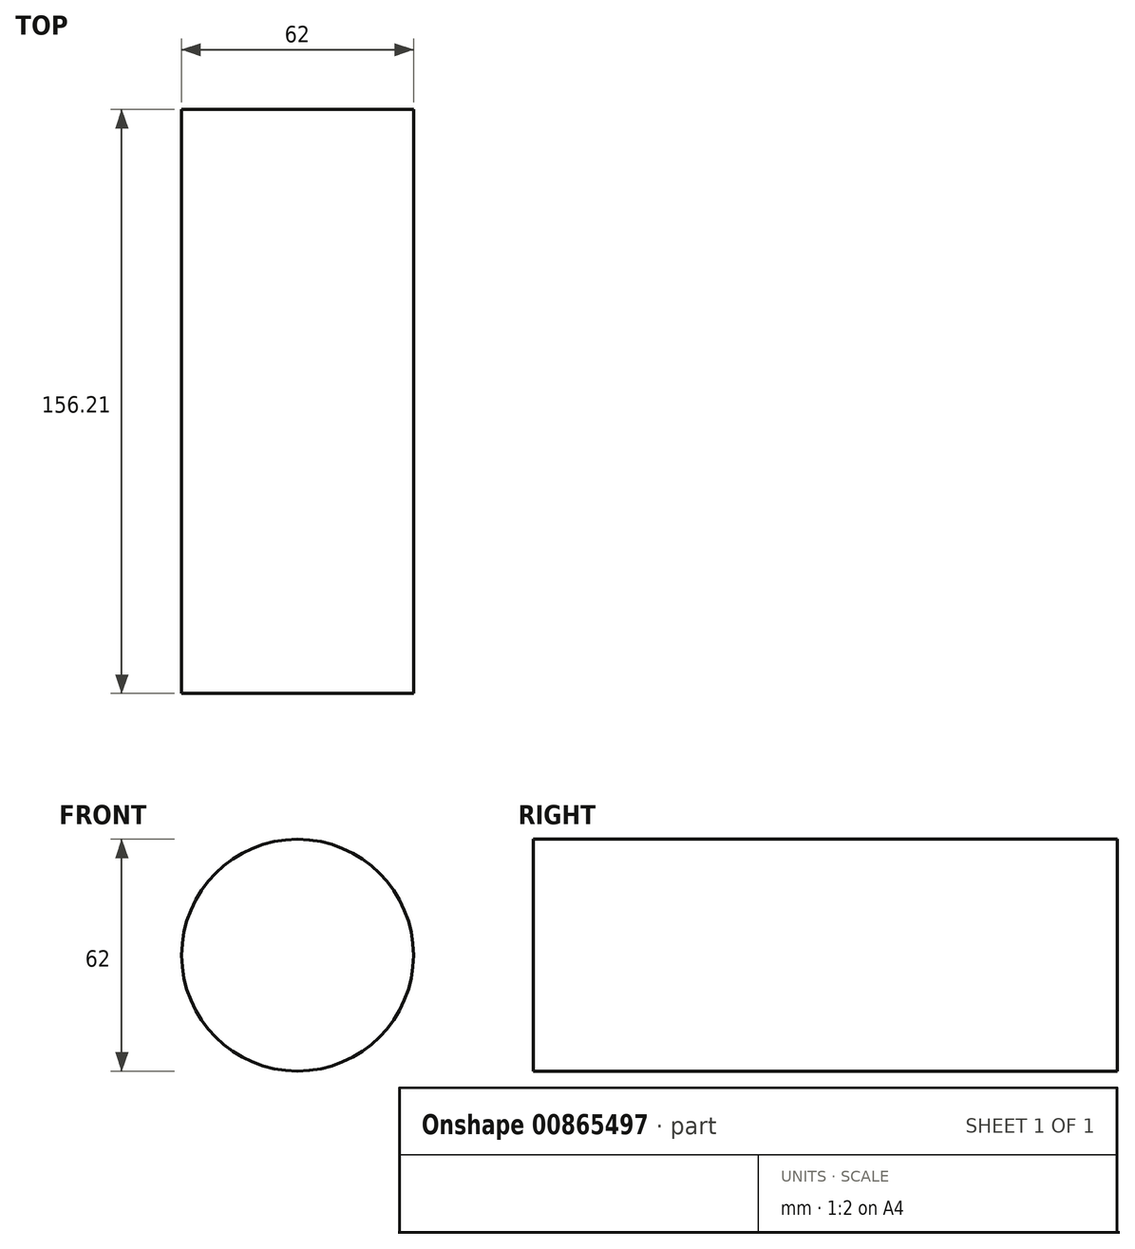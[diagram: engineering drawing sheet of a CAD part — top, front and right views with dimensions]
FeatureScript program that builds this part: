
annotation { "Feature Type Name" : "Feature", "Feature Type Description" : "" }
export const myFeature = defineFeature(function(context is Context, id is Id, definition is map)
    precondition{}
    {
        {
            var Q0;
            Q0=qCreatedBy(makeId("Front.planeOp"),FACE);
            var sketch = newSketch(context, id + "F0", { "sketchPlane" : qUnion([Q0])});
            skCircle(sketch, "E0", {"center": v(0, 0) * mm, "radius": 31 * mm});
            skSolve(sketch);
        }
        {
            var Q0;
            Q0=makeQuery(id+"F0.imprint","IMPRINT",FACE,{"disambiguationData":[TD([[makeQuery(id+"F0.imprint","IMPRINT",EDGE,{"derivedFrom":sQuery(id+"F0.wireOp",EDGE,"E0")}),1.0]])]});
            extrude(context, id + "F1", {"entities" : qUnion([Q0]), "depth" : 156.2 * mm, "offsetDistance" : 25.4 * mm});
        }
    });
